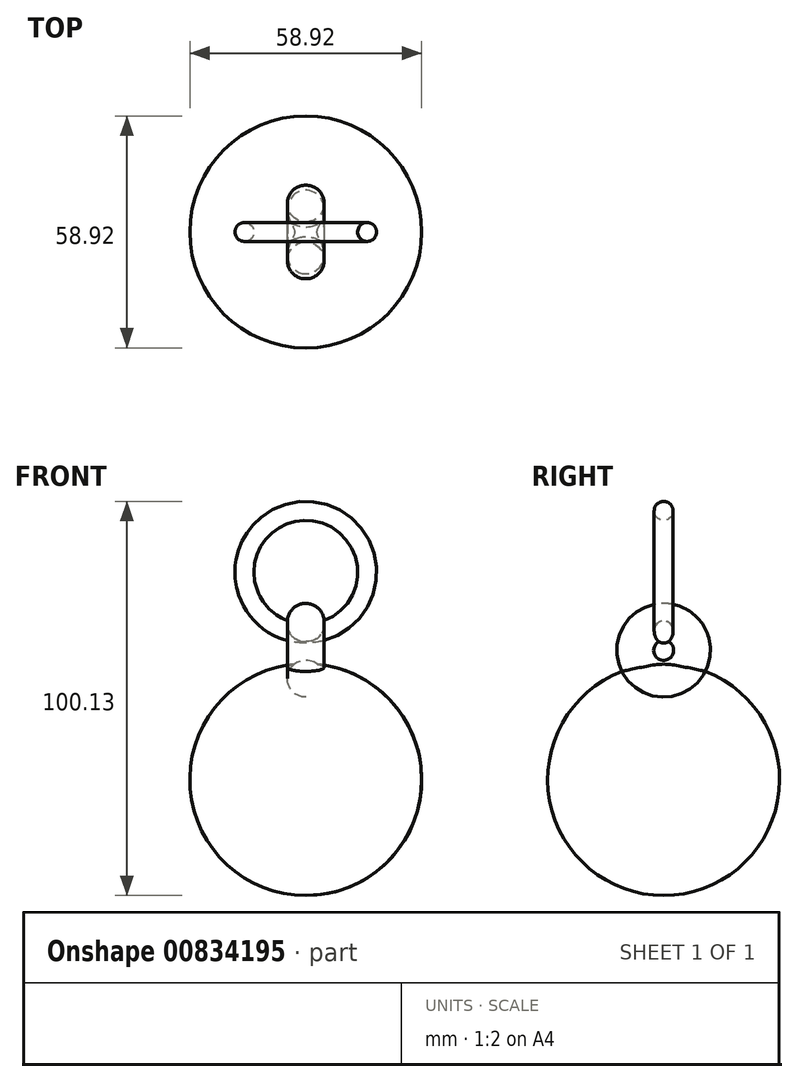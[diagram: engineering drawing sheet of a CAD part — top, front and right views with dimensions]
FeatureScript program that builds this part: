
annotation { "Feature Type Name" : "Feature", "Feature Type Description" : "" }
export const myFeature = defineFeature(function(context is Context, id is Id, definition is map)
    precondition{}
    {
        {
            var Q0;
            Q0=qCreatedBy(makeId("Front.planeOp"),FACE);
            var sketch = newSketch(context, id + "F0", { "sketchPlane" : qUnion([Q0])});
            skArc(sketch, "E0", {"start": v(0, -69.54) * mm, "mid": v(-29.46, -40.08) * mm, "end": v(0, -10.62) * mm});
            skLineSegment(sketch, "E1", {"start": v(0, 21.67) * mm, "end": v(0, -73.8) * mm});
            skSolve(sketch);
        }
        {
            var Q0;
            Q0 = qSketchRegion(id + "F0", true);
            var Q1;
            Q1=sQuery(id+"F0.wireOp",EDGE,"E1");
            revolve(context, id + "F1", {"surfaceOperationType" : NewSurfaceOperationType.NEW, "entities" : qUnion([Q0]), "axis" : qUnion([Q1]), "revolveType" : RevolveType.FULL});
        }
        {
            var Q0;
            Q0=qCreatedBy(makeId("Front.planeOp"),FACE);
            var sketch = newSketch(context, id + "F2", { "sketchPlane" : qUnion([Q0])});
            skLineSegment(sketch, "E2", {"start": v(0, -7.22) * mm, "end": v(23.37, -7.22) * mm});
            skLineSegment(sketch, "E3", {"start": v(23.37, -7.22) * mm, "end": v(-23.09, -7.22) * mm});
            skCircle(sketch, "E4", {"center": v(0, 0) * mm, "radius": 4.68 * mm});
            skSolve(sketch);
        }
        {
            var Q0;
            Q0 = qSketchRegion(id + "F2", true);
            var Q1;
            Q1=sQuery(id+"F2.wireOp",EDGE,"E3");
            revolve(context, id + "F3", {"operationType" : NewBodyOperationType.ADD, "surfaceOperationType" : NewSurfaceOperationType.NEW, "entities" : qUnion([Q0]), "axis" : qUnion([Q1]), "revolveType" : RevolveType.FULL});
        }
        {
            var Q0;
            Q0=qCreatedBy(makeId("Right.planeOp"),FACE);
            var sketch = newSketch(context, id + "F4", { "sketchPlane" : qUnion([Q0])});
            skLineSegment(sketch, "E5", {"start": v(0, 12.6) * mm, "end": v(9.77, 12.6) * mm});
            skLineSegment(sketch, "E6", {"start": v(9.77, 12.6) * mm, "end": v(-11.19, 12.6) * mm});
            skCircle(sketch, "E7", {"center": v(0, 28.19) * mm, "radius": 2.4 * mm});
            skSolve(sketch);
        }
        {
            var Q0;
            Q0 = qSketchRegion(id + "F4", true);
            var Q1;
            Q1=sQuery(id+"F4.wireOp",EDGE,"E6");
            revolve(context, id + "F5", {"operationType" : NewBodyOperationType.ADD, "surfaceOperationType" : NewSurfaceOperationType.NEW, "entities" : qUnion([Q0]), "axis" : qUnion([Q1]), "revolveType" : RevolveType.FULL});
        }
    });
